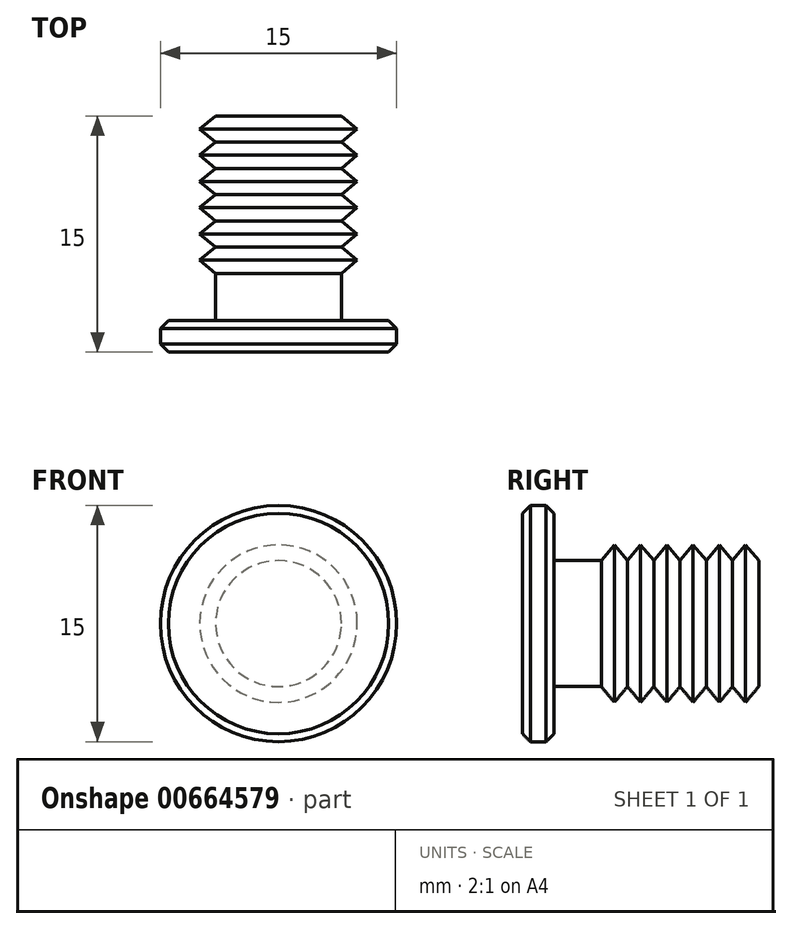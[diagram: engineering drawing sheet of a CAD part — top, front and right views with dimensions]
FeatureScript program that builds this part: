
annotation { "Feature Type Name" : "Feature", "Feature Type Description" : "" }
export const myFeature = defineFeature(function(context is Context, id is Id, definition is map)
    precondition{}
    {
        {
            var Q0;
            Q0=qCreatedBy(makeId("Top.planeOp"),FACE);
            var sketch = newSketch(context, id + "F0", { "sketchPlane" : qUnion([Q0])});
            skLineSegment(sketch, "E0", {"start": v(0, 0) * mm, "end": v(0, 32.75) * mm, "construction": true});
            skLineSegment(sketch, "E1", {"start": v(0, 0) * mm, "end": v(7, 0) * mm});
            skLineSegment(sketch, "E2", {"start": v(7, 0) * mm, "end": v(7.5, 0.5) * mm});
            skLineSegment(sketch, "E3", {"start": v(7.5, 0.5) * mm, "end": v(7.5, 1.5) * mm});
            skLineSegment(sketch, "E4", {"start": v(7.5, 1.5) * mm, "end": v(7, 2) * mm});
            skLineSegment(sketch, "E5", {"start": v(7, 2) * mm, "end": v(4, 2) * mm});
            skLineSegment(sketch, "E6", {"start": v(4, 2) * mm, "end": v(4, 5) * mm});
            skLineSegment(sketch, "E7", {"start": v(4, 5) * mm, "end": v(5, 5.83) * mm});
            skLineSegment(sketch, "E8", {"start": v(5, 5.83) * mm, "end": v(4, 6.67) * mm});
            skLineSegment(sketch, "E9", {"start": v(4, 6.67) * mm, "end": v(5, 7.5) * mm});
            skLineSegment(sketch, "E10", {"start": v(5, 7.5) * mm, "end": v(4, 8.33) * mm});
            skLineSegment(sketch, "E11", {"start": v(4, 8.33) * mm, "end": v(5, 9.17) * mm});
            skLineSegment(sketch, "E12", {"start": v(5, 9.17) * mm, "end": v(4, 10) * mm});
            skLineSegment(sketch, "E13", {"start": v(4, 10) * mm, "end": v(5, 10.83) * mm});
            skLineSegment(sketch, "E14", {"start": v(5, 10.83) * mm, "end": v(4, 11.67) * mm});
            skLineSegment(sketch, "E15", {"start": v(4, 11.67) * mm, "end": v(5, 12.5) * mm});
            skLineSegment(sketch, "E16", {"start": v(5, 12.5) * mm, "end": v(4, 13.33) * mm});
            skLineSegment(sketch, "E17", {"start": v(4, 13.33) * mm, "end": v(5, 14.17) * mm});
            skLineSegment(sketch, "E18", {"start": v(5, 14.17) * mm, "end": v(4, 15) * mm});
            skLineSegment(sketch, "E19", {"start": v(4, 15) * mm, "end": v(0, 15) * mm});
            skLineSegment(sketch, "E20", {"start": v(0, 15) * mm, "end": v(0, 0) * mm});
            skSolve(sketch);
        }
        {
            var Q0;
            Q0 = qSketchRegion(id + "F0", true);
            var Q1;
            Q1=sQuery(id+"F0.wireOp",EDGE,"E0");
            revolve(context, id + "F1", {"entities" : qUnion([Q0]), "axis" : qUnion([Q1]), "revolveType" : RevolveType.FULL});
        }
    });
